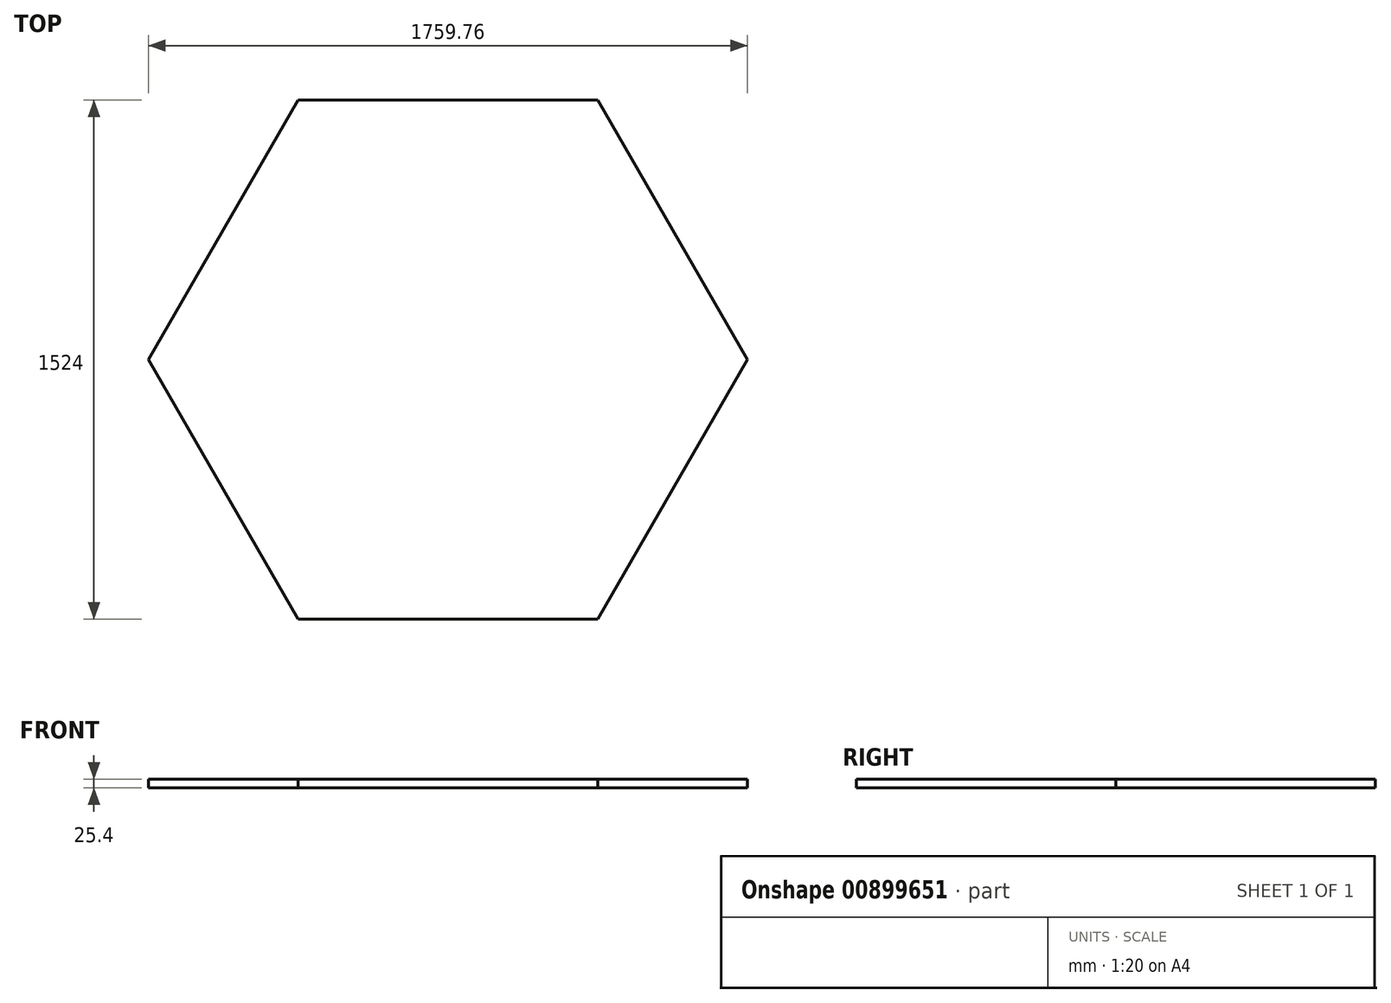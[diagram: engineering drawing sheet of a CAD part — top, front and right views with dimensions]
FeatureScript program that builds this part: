
annotation { "Feature Type Name" : "Feature", "Feature Type Description" : "" }
export const myFeature = defineFeature(function(context is Context, id is Id, definition is map)
    precondition{}
    {
        {
            var Q0;
            Q0=qCreatedBy(makeId("Top.planeOp"),FACE);
            var sketch = newSketch(context, id + "F0", { "sketchPlane" : qUnion([Q0])});
            skCircle(sketch, "E0.cCircle", {"center": v(0, 0) * mm, "radius": 879.88 * mm, "construction": true});
            skLineSegment(sketch, "E0.0", {"start": v(879.88, 0) * mm, "end": v(439.94, -762) * mm});
            skLineSegment(sketch, "E0.1", {"start": v(439.94, -762) * mm, "end": v(-439.94, -762) * mm});
            skLineSegment(sketch, "E0.2", {"start": v(-439.94, -762) * mm, "end": v(-879.88, 0) * mm});
            skLineSegment(sketch, "E0.3", {"start": v(-879.88, 0) * mm, "end": v(-439.94, 762) * mm});
            skLineSegment(sketch, "E0.4", {"start": v(-439.94, 762) * mm, "end": v(439.94, 762) * mm});
            skLineSegment(sketch, "E0.5", {"start": v(439.94, 762) * mm, "end": v(879.88, 0) * mm});
            skSolve(sketch);
        }
        {
            var Q0;
            Q0=makeQuery(id+"F0.imprint","IMPRINT",FACE,{"disambiguationData":[TD([[makeQuery(id+"F0.imprint","IMPRINT",EDGE,{"derivedFrom":sQuery(id+"F0.wireOp",EDGE,"E0.0")}),-1.0]])]});
            extrude(context, id + "F1", {"entities" : qUnion([Q0]), "depth" : 25.4 * mm, "offsetDistance" : 25.4 * mm});
        }
    });
